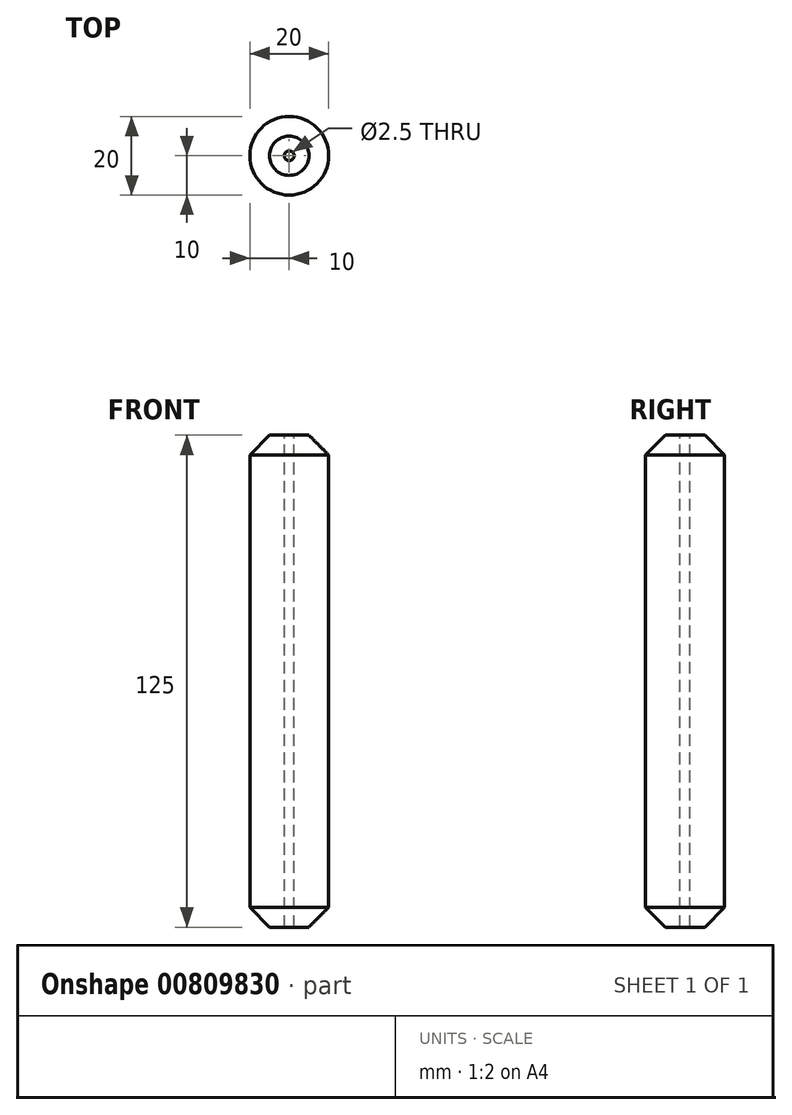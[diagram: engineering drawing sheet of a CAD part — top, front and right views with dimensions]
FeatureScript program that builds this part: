
annotation { "Feature Type Name" : "Feature", "Feature Type Description" : "" }
export const myFeature = defineFeature(function(context is Context, id is Id, definition is map)
    precondition{}
    {
        {
            var Q0;
            Q0=qCreatedBy(makeId("Top.planeOp"),FACE);
            var sketch = newSketch(context, id + "F0", { "sketchPlane" : qUnion([Q0])});
            skCircle(sketch, "E0", {"center": v(0, 0) * mm, "radius": 10 * mm});
            skSolve(sketch);
        }
        {
            var Q0;
            Q0=makeQuery(id+"F0.imprint","IMPRINT",FACE,{"disambiguationData":[TD([[makeQuery(id+"F0.imprint","IMPRINT",EDGE,{"derivedFrom":sQuery(id+"F0.wireOp",EDGE,"E0")}),1.0]])]});
            extrude(context, id + "F1", {"entities" : qUnion([Q0]), "depth" : 100 * mm, "offsetDistance" : 25 * mm, "hasSecondDirection" : true, "secondDirectionOppositeDirection" : true, "secondDirectionDepth" : 25 * mm});
        }
        {
            var Q0;
            Q0=makeQuery(id+"F1.opExtrude","CAP_EDGE",EDGE,{"disambiguationData":[OSD([sQuery(id+"F0.wireOp",EDGE,"E0")])],"isStart":false});
            chamfer(context, id + "F2", {"entities" : qUnion([Q0]), "width" : 5 * mm, "tangentPropagation" : true});
        }
        {
            var Q0;
            Q0=makeQuery(id+"F1.opExtrude","CAP_FACE",FACE,{"disambiguationData":[OSD([sQuery(id+"F0.wireOp",EDGE,"E0")])],"isStart":false});
            var sketch = newSketch(context, id + "F3", { "sketchPlane" : qUnion([Q0])});
            skPoint(sketch, "E1", {"position": v(0, 0) * mm});
            skCircle(sketch, "E2", {"center": v(0, 0) * mm, "radius": 1.38 * mm});
            skSolve(sketch);
        }
        {
            var Q0;
            Q0=sQuery(id+"F3.wireOp",VERTEX,"E1");
            var Q1;
            Q1=makeQuery(id+"F1.opExtrude","SWEPT_BODY",BODY,{"disambiguationData":[OSD([sQuery(id+"F0.wireOp",EDGE,"E0")])]});
            hole(context, id + "F4", {"style" : HoleStyle.SIMPLE, "endStyle" : HoleEndStyle.THROUGH, "standardTappedOrClearance" : lookupTablePath({ "standard" : "ISO", "engagement" : "75%", "pitch" : "0.5 mm", "size" : "M3", "type" : "Tapped" }), "standardBlindInLast" : lookupTablePath({ "standard" : "ISO", "engagement" : "75%", "pitch" : "0.5 mm", "size" : "M3", "type" : "Tapped" }), "holeDiameter" : 2.5 * mm, "majorDiameter" : 3 * mm, "showTappedDepth" : true, "isTappedThrough" : true, "tappedDepth" : 12 * mm, "tapClearance" : 3, "locations" : qUnion([Q0]), "scope" : qUnion([Q1])});
        }
        {
            var Q0;
            Q0=makeQuery(id+"F1.opExtrude","CAP_EDGE",EDGE,{"disambiguationData":[OSD([sQuery(id+"F0.wireOp",EDGE,"E0")])],"isStart":true});
            chamfer(context, id + "F5", {"entities" : qUnion([Q0]), "width" : 5 * mm, "tangentPropagation" : true});
        }
    });
